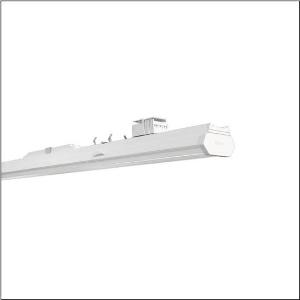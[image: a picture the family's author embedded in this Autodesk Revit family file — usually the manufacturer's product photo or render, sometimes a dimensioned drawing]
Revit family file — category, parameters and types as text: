
# Revit family: licross_r__21_protected_ho_52td12dn4e5m3s4_bb7a
name_source: partatom
category: Lighting Fixtures
units: mm (PartAtom-declared; Revit-internal decimal feet)

## family parameters
Cut with Voids When Loaded = No
Host = Face
Light Source = No
Part Type = Normal
Room Calculation Point = No
Round Connector Dimension = Use Diameter
Shared = No

## types (1)
- --- (1 x LED, 910 lm, 7.6 W, 4000K)
    Apparent Load = 8 VA
    CIE Flux Codes = 70 91 97 98 100
    Color Rendering = 80
    Color Temperature = 4000K
    Default Elevation = 1800 mm
    Description = Licross® 21 Protected HO, luminaire insert, of sheet steel, galvanised, coil coated, white, length: 1.500mm, width: 90mm, height: 103mm, LED rated luminous flux: 14.690lm, light colour: 840, control gear: DALI 2, with plug, 6-pole, with phase selection, for trunking rail, 9 or 11-core, mains connection: 220..240V, AC, 50/60Hz, rated input power: 89W, for trunking rail, 9-/11-core, halogen-free wiring, for emergency light function, converter,control gear: single battery element, battery: LiFeP04, 9Ah, primary light control with lens, of plastic, primary optical cover: cover, of PMMA, light emission: direct distribution, primary light characteristic: symmetric, protection rating (complete): IP54, insulation class (complete): insulation class I (protective earthing), certification: CE, UKCA, protection symbol: D if used in an environment with non-conductive dust loads with corresponding accessories, impact resistance: IK06, permissible ambient temperature for indoor applications: +5..+30°C, standard: EN 60598-2-22, LABS conformity tested according to VDMA 24364:2018-05, reducing of maximum allowable ambient temperature of 5°C with ceiling mounting, corresponds to IFS (International Featured Standards) requirements for safety and quality in the food industry, packaging unit: 1 piece
    Height = 92 mm
    Lamp = 1 x LED
    Lamp Light Flux = 910 lm
    Lamp Power = 7.6 W
    Lamp count = 1
    Length = 1500 mm
    Luminous efficacy = 120 lm/W
    Manufacturer = Siteco
    ModVariant = No
    Model = 52TD12DN4E5M3S4
    Mounting Place = Ceiling
    Mounting Type = Pendant
    Number of Poles = 1
    OnlyDefault = Yes
    Power Factor = 1
    Product Name = Licross® 21 Protected HO
    Product group = luminaire insert
    ProductGroupID = 901
    Protection Class = Protection class I
    Protection Degree = IP 54
    RLX_Detail_Level = 1
    RLX_Emergency_Light_Flux = 0 lm
    RLX_Emergency_Type = 0
    RLX_Emergency_Type_DB = No
    RlxData = <blob elided: 24961 chars, md5=a28918a8>
    Socket = socket
    Standby Power = 0 W
    System Light Flux = 910 lm
    System Power = 8 W
    Type Comments = : emergency light operation: 3 h
    Type Image = l_1256148.jpg
    URL = http://relux.com
    VarID = @adj_041307
    Voltage = 0 V
    Weight = 0.00 kg
    Width = 88 mm

## geometry (parser evidence)
native form markers: Blend x4, Sweep x9
no freeform markers — native parametric forms only
